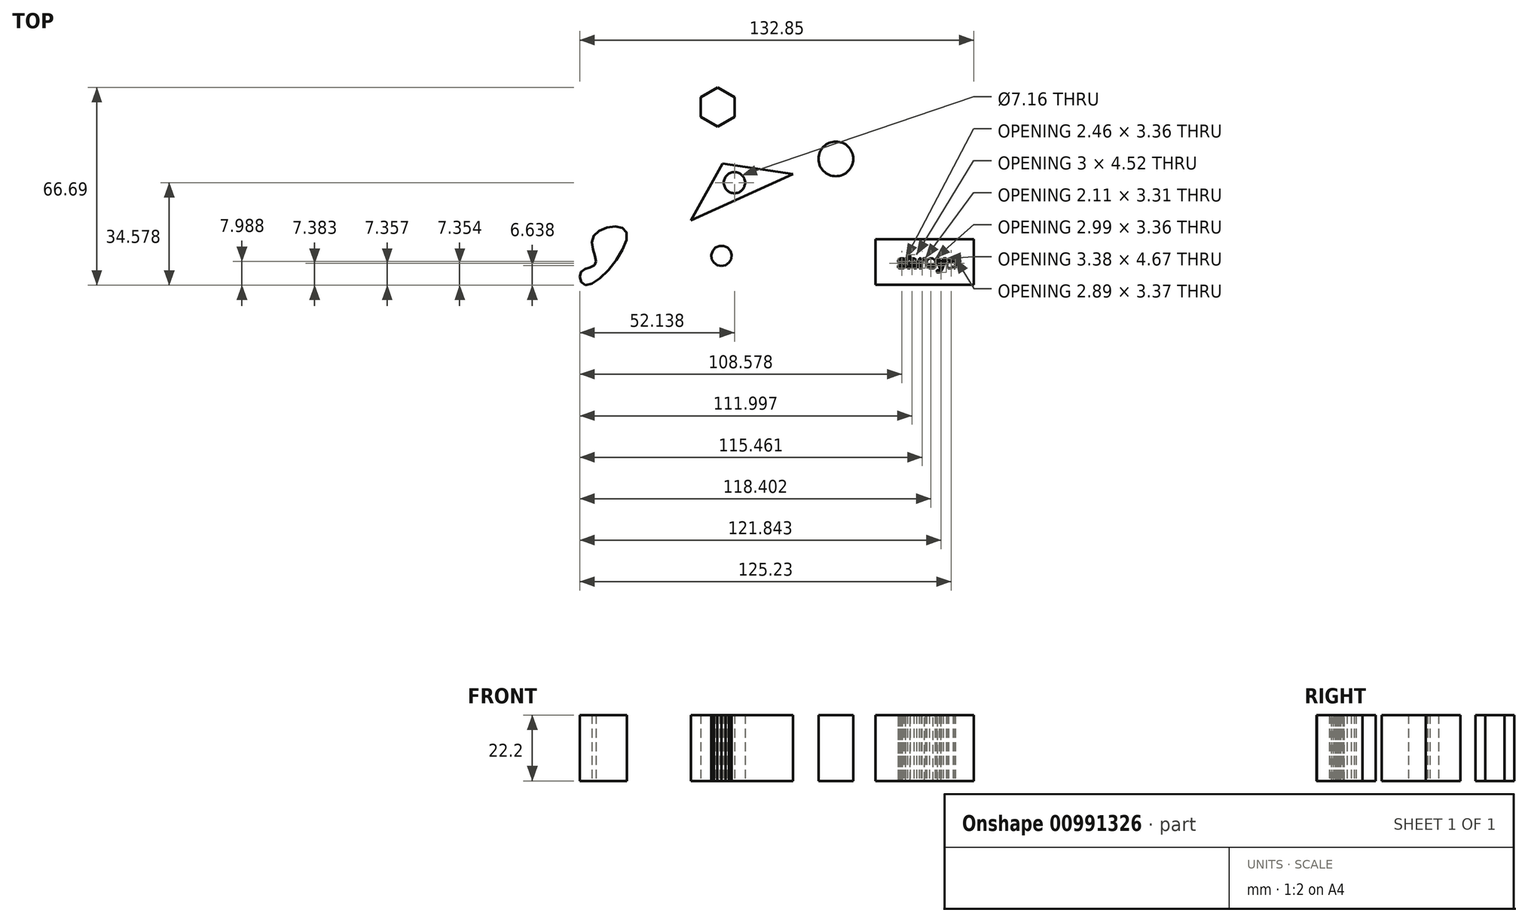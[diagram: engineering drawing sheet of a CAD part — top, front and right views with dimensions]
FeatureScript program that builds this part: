
annotation { "Feature Type Name" : "Feature", "Feature Type Description" : "" }
export const myFeature = defineFeature(function(context is Context, id is Id, definition is map)
    precondition{}
    {
        {
            var Q0;
            Q0=qCreatedBy(makeId("Top.planeOp"),FACE);
            var sketch = newSketch(context, id + "F0", { "sketchPlane" : qUnion([Q0])});
            skLineSegment(sketch, "E0", {"start": v(-36.5, 21.82) * mm, "end": v(-12.81, 18.25) * mm});
            skLineSegment(sketch, "E1", {"start": v(-12.81, 18.25) * mm, "end": v(-47.2, 2.67) * mm});
            skLineSegment(sketch, "E2", {"start": v(-47.2, 2.67) * mm, "end": v(-36.5, 21.82) * mm});
            skLineSegment(sketch, "E3.bottom", {"start": v(15.02, -3.76) * mm, "end": v(48.22, -3.76) * mm});
            skLineSegment(sketch, "E3.top", {"start": v(15.02, -19.13) * mm, "end": v(48.22, -19.13) * mm});
            skLineSegment(sketch, "E3.left", {"start": v(15.02, -3.76) * mm, "end": v(15.02, -19.13) * mm});
            skLineSegment(sketch, "E3.right", {"start": v(48.22, -3.76) * mm, "end": v(48.22, -19.13) * mm});
            skCircle(sketch, "E4", {"center": v(1.7, 23.37) * mm, "radius": 5.84 * mm});
            skArc(sketch, "E5", {"start": v(-44.1, 27.42) * mm, "mid": v(-51.03, 28.96) * mm, "end": v(-50.06, 21.94) * mm});
            skCircle(sketch, "E6.cCircle", {"center": v(-38.16, 40.86) * mm, "radius": 5.71 * mm, "construction": true});
            skLineSegment(sketch, "E6.0", {"start": v(-32.45, 44.16) * mm, "end": v(-32.45, 37.57) * mm});
            skLineSegment(sketch, "E6.1", {"start": v(-32.45, 37.57) * mm, "end": v(-38.16, 34.27) * mm});
            skLineSegment(sketch, "E6.2", {"start": v(-38.16, 34.27) * mm, "end": v(-43.87, 37.57) * mm});
            skLineSegment(sketch, "E6.3", {"start": v(-43.87, 37.57) * mm, "end": v(-43.87, 44.16) * mm});
            skLineSegment(sketch, "E6.4", {"start": v(-43.87, 44.16) * mm, "end": v(-38.16, 47.46) * mm});
            skLineSegment(sketch, "E6.5", {"start": v(-38.16, 47.46) * mm, "end": v(-32.45, 44.16) * mm});
            skPoint(sketch, "E6.0.midPoint", {"position": v(-32.45, 40.86) * mm});
            skCircle(sketch, "E7.cCircle", {"center": v(-36.85, -9.35) * mm, "radius": 3.37 * mm, "construction": true});
            skLineSegment(sketch, "E7.0", {"start": v(-34.83, -6.56) * mm, "end": v(-33.87, -7.62) * mm});
            skLineSegment(sketch, "E7.1", {"start": v(-33.87, -7.62) * mm, "end": v(-33.43, -8.98) * mm});
            skLineSegment(sketch, "E7.2", {"start": v(-33.43, -8.98) * mm, "end": v(-33.57, -10.4) * mm});
            skLineSegment(sketch, "E7.3", {"start": v(-33.57, -10.4) * mm, "end": v(-34.29, -11.65) * mm});
            skLineSegment(sketch, "E7.4", {"start": v(-34.29, -11.65) * mm, "end": v(-35.44, -12.5) * mm});
            skLineSegment(sketch, "E7.5", {"start": v(-35.44, -12.5) * mm, "end": v(-36.84, -12.8) * mm});
            skLineSegment(sketch, "E7.6", {"start": v(-36.84, -12.8) * mm, "end": v(-38.25, -12.5) * mm});
            skLineSegment(sketch, "E7.7", {"start": v(-38.25, -12.5) * mm, "end": v(-39.4, -11.66) * mm});
            skLineSegment(sketch, "E7.8", {"start": v(-39.4, -11.66) * mm, "end": v(-40.13, -10.42) * mm});
            skLineSegment(sketch, "E7.9", {"start": v(-40.13, -10.42) * mm, "end": v(-40.28, -9) * mm});
            skLineSegment(sketch, "E7.10", {"start": v(-40.28, -9) * mm, "end": v(-39.84, -7.64) * mm});
            skLineSegment(sketch, "E7.11", {"start": v(-39.84, -7.64) * mm, "end": v(-38.88, -6.57) * mm});
            skLineSegment(sketch, "E7.12", {"start": v(-38.88, -6.57) * mm, "end": v(-37.58, -5.98) * mm});
            skLineSegment(sketch, "E7.13", {"start": v(-37.58, -5.98) * mm, "end": v(-36.14, -5.98) * mm});
            skLineSegment(sketch, "E7.14", {"start": v(-36.14, -5.98) * mm, "end": v(-34.83, -6.56) * mm});
            skPoint(sketch, "E7.0.midPoint", {"position": v(-34.35, -7.1) * mm});
            skFitSpline(sketch, "E8", {"points": [v(-84.21, -14.83) * mm, v(-79.33, -11.97) * mm, v(-80.05, -2.69) * mm, v(-68.98, -1.14) * mm, v(-82.3, -19.23) * mm, v(-84.21, -14.83) * mm]});
            skText(sketch, "E9", { "text": "shreya", "fontName": "OpenSans-Bold.ttf"});
            const initialGuessF0  = {"E9": [0.02245, -0.0135, 1, 0, 0.00428]};
            skSetInitialGuess(sketch, initialGuessF0);
            skSolve(sketch);
        }
        {
            var Q0;
            Q0 = qSketchRegion(id + "F0", true);
            extrude(context, id + "F1", {"entities" : qUnion([Q0]), "depth" : 22.2 * mm, "offsetDistance" : 25 * mm});
        }
        {
            var Q0;
            Q0=qCreatedBy(makeId("Top.planeOp"),FACE);
            var sketch = newSketch(context, id + "F2", { "sketchPlane" : qUnion([Q0])});
            skCircle(sketch, "E10", {"center": v(-32.5, 15.35) * mm, "radius": 3.58 * mm});
            skSolve(sketch);
        }
        {
            var Q0;
            Q0 = qSketchRegion(id + "F2", true);
            extrude(context, id + "F3", {"entities" : qUnion([Q0]), "operationType" : NewBodyOperationType.REMOVE, "depth" : 35 * mm, "offsetDistance" : 25 * mm});
        }
    });
